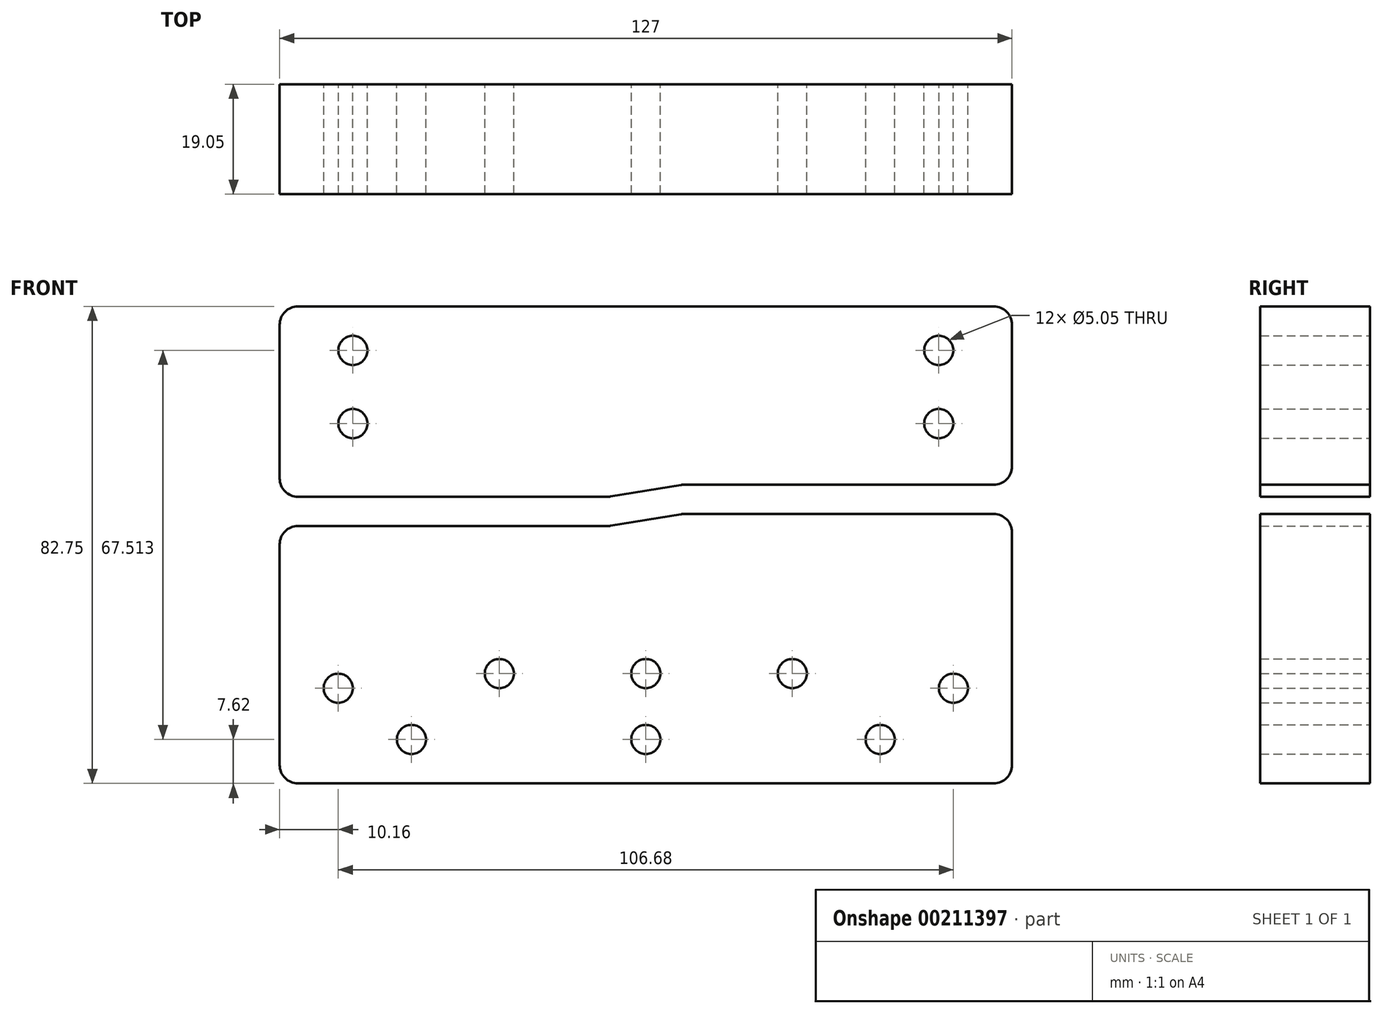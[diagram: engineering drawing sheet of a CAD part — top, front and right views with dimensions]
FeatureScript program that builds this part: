
annotation { "Feature Type Name" : "Feature", "Feature Type Description" : "" }
export const myFeature = defineFeature(function(context is Context, id is Id, definition is map)
    precondition{}
    {
        {
            var Q0;
            Q0=qCreatedBy(makeId("Front.planeOp"),FACE);
            var sketch = newSketch(context, id + "F0", { "sketchPlane" : qUnion([Q0])});
            skLineSegment(sketch, "E0.top", {"start": v(-60.33, 0) * mm, "end": v(60.33, 0) * mm});
            skLineSegment(sketch, "E0.left", {"start": v(-63.5, 41.48) * mm, "end": v(-63.5, 3.17) * mm});
            skLineSegment(sketch, "E0.right", {"start": v(63.5, 43.56) * mm, "end": v(63.5, 3.18) * mm});
            skLineSegment(sketch, "E1.top", {"start": v(-60.33, 82.75) * mm, "end": v(60.32, 82.75) * mm});
            skLineSegment(sketch, "E1.left", {"start": v(-63.5, 52.9) * mm, "end": v(-63.5, 79.58) * mm});
            skLineSegment(sketch, "E1.right", {"start": v(63.5, 55) * mm, "end": v(63.5, 79.58) * mm});
            skCircle(sketch, "E2", {"center": v(0, 19.05) * mm, "radius": 2.53 * mm});
            skCircle(sketch, "E3", {"center": v(-53.34, 16.5) * mm, "radius": 2.53 * mm});
            skCircle(sketch, "E4", {"center": v(-25.4, 19.05) * mm, "radius": 2.53 * mm});
            skCircle(sketch, "E5", {"center": v(25.4, 19.05) * mm, "radius": 2.53 * mm});
            skCircle(sketch, "E6", {"center": v(53.34, 16.5) * mm, "radius": 2.53 * mm});
            skCircle(sketch, "E7", {"center": v(-40.64, 7.62) * mm, "radius": 2.53 * mm});
            skCircle(sketch, "E8", {"center": v(40.64, 7.62) * mm, "radius": 2.53 * mm});
            skCircle(sketch, "E9", {"center": v(0, 7.62) * mm, "radius": 2.53 * mm});
            skCircle(sketch, "E10", {"center": v(-50.8, 75.13) * mm, "radius": 2.53 * mm});
            skCircle(sketch, "E11", {"center": v(50.8, 75.13) * mm, "radius": 2.53 * mm});
            skCircle(sketch, "E12", {"center": v(-50.8, 62.43) * mm, "radius": 2.53 * mm});
            skCircle(sketch, "E13", {"center": v(50.8, 62.43) * mm, "radius": 2.53 * mm});
            skPoint(sketch, "E14.visualSharp", {"position": v(-63.5, 44.65) * mm});
            skPoint(sketch, "E15.visualSharp", {"position": v(63.5, 38.1) * mm});
            skPoint(sketch, "E16.visualSharp", {"position": v(-63.5, 50.3) * mm});
            skPoint(sketch, "E17.visualSharp", {"position": v(63.5, 49.7) * mm});
            skPoint(sketch, "E18.visualSharp", {"position": v(-63.5, 82.75) * mm});
            skArc(sketch, "E18.filletArc", {"start": v(-60.33, 82.75) * mm, "mid": v(-62.57, 81.82) * mm, "end": v(-63.5, 79.58) * mm});
            skPoint(sketch, "E19.visualSharp", {"position": v(63.5, 82.75) * mm});
            skArc(sketch, "E19.filletArc", {"start": v(63.5, 79.58) * mm, "mid": v(62.57, 81.82) * mm, "end": v(60.32, 82.75) * mm});
            skPoint(sketch, "E20.visualSharp", {"position": v(63.5, 0) * mm});
            skArc(sketch, "E20.filletArc", {"start": v(60.33, 0) * mm, "mid": v(62.57, 0.93) * mm, "end": v(63.5, 3.18) * mm});
            skPoint(sketch, "E21.visualSharp", {"position": v(-63.5, 0) * mm});
            skArc(sketch, "E21.filletArc", {"start": v(-63.5, 3.17) * mm, "mid": v(-62.57, 0.93) * mm, "end": v(-60.33, 0) * mm});
            skLineSegment(sketch, "E22", {"start": v(6.6, 46.74) * mm, "end": v(60.33, 46.74) * mm});
            skLineSegment(sketch, "E23", {"start": v(-60.33, 44.65) * mm, "end": v(-6.6, 44.65) * mm});
            skLineSegment(sketch, "E24", {"start": v(-6.1, 44.7) * mm, "end": v(6.1, 46.7) * mm});
            skPoint(sketch, "E25.visualSharp", {"position": v(-6.35, 44.65) * mm});
            skArc(sketch, "E25.filletArc", {"start": v(-6.6, 44.65) * mm, "mid": v(-6.35, 44.66) * mm, "end": v(-6.1, 44.7) * mm});
            skPoint(sketch, "E26.visualSharp", {"position": v(6.35, 46.74) * mm});
            skArc(sketch, "E26.filletArc", {"start": v(6.6, 46.74) * mm, "mid": v(6.35, 46.73) * mm, "end": v(6.1, 46.7) * mm});
            skLineSegment(sketch, "E27", {"start": v(-60.32, 49.73) * mm, "end": v(-6.6, 49.73) * mm});
            skLineSegment(sketch, "E28", {"start": v(-6.1, 49.78) * mm, "end": v(6.1, 51.77) * mm});
            skLineSegment(sketch, "E29", {"start": v(6.6, 51.82) * mm, "end": v(60.33, 51.82) * mm});
            skPoint(sketch, "E30.visualSharp", {"position": v(-6.35, 49.73) * mm});
            skArc(sketch, "E30.filletArc", {"start": v(-6.6, 49.73) * mm, "mid": v(-6.35, 49.74) * mm, "end": v(-6.1, 49.78) * mm});
            skPoint(sketch, "E31.visualSharp", {"position": v(6.35, 51.82) * mm});
            skArc(sketch, "E31.filletArc", {"start": v(6.6, 51.82) * mm, "mid": v(6.35, 51.8) * mm, "end": v(6.1, 51.77) * mm});
            skPoint(sketch, "E32.visualSharp", {"position": v(-63.5, 49.73) * mm});
            skArc(sketch, "E32.filletArc", {"start": v(-63.5, 52.9) * mm, "mid": v(-62.57, 50.66) * mm, "end": v(-60.32, 49.73) * mm});
            skPoint(sketch, "E33.visualSharp", {"position": v(63.5, 51.82) * mm});
            skArc(sketch, "E33.filletArc", {"start": v(60.33, 51.82) * mm, "mid": v(62.57, 52.75) * mm, "end": v(63.5, 55) * mm});
            skPoint(sketch, "E34.visualSharp", {"position": v(63.5, 46.74) * mm});
            skArc(sketch, "E34.filletArc", {"start": v(63.5, 43.56) * mm, "mid": v(62.57, 45.8) * mm, "end": v(60.33, 46.74) * mm});
            skArc(sketch, "E35.filletArc", {"start": v(-60.33, 44.65) * mm, "mid": v(-62.57, 43.72) * mm, "end": v(-63.5, 41.48) * mm});
            skSolve(sketch);
        }
        {
            var Q0;
            {var subQ0=sQuery(id+"F0.wireOp",EDGE,"E0.top");Q0=makeQuery(id+"F0.imprint","IMPRINT",FACE,{"disambiguationData":[TD([[makeQuery(id+"F0.imprint","IMPRINT",EDGE,{"derivedFrom":subQ0}),1.0]])]});}
            var Q1;
            Q1=makeQuery(id+"F0.imprint","IMPRINT",FACE,{"disambiguationData":[TD([[makeQuery(id+"F0.imprint","IMPRINT",EDGE,{"derivedFrom":sQuery(id+"F0.wireOp",EDGE,"E1.top")}),-1.0]])]});
            extrude(context, id + "F1", {"entities" : qUnion([Q0, Q1]), "depth" : 19.05 * mm});
        }
    });
